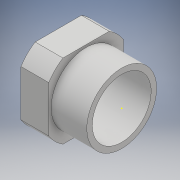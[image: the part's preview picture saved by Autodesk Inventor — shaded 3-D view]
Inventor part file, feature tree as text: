
AUTODESK INVENTOR PART (.ipt)
format: ipt  version: 2018 (Build 220112000, 112)  size: 135,680 bytes
history: native  units: mm
features: sketch x8, extrude x5
ambient origin geometry x8: Origin, YZ Plane, XZ Plane, XY Plane, X Axis, Y Axis, Z Axis, Center Point
bodies: Solid1 (feature_tree)
feature tree (13):
  extrude  "Extrusion1"  Depth=20.4mm
  extrude  "Extrusion2"  Depth=7.6mm
  extrude  "Extrusion3"  Depth=7.6mm
  extrude  "Extrusion4"  Depth=9.75mm
  sketch  "Sketch5"  dims[d11=12.75mm d12=0.0mm d13=6.35mm]
  sketch  "Sketch6"  dims[d14=12.75mm d15=0.0mm]
  extrude  "Extrusion5"  Depth=12.75mm
  sketch  "Sketch8"
  sketch  "Sketch1"  dims[d0=20.4mm d1=20.4mm]
  sketch  "Sketch2"  dims[d2=7.6mm d3=0.0mm d4=24.0mm]
  sketch  "Sketch3"  dims[d5=7.6mm d6=0.0mm d7=19.1mm]
  sketch  "Sketch4"  dims[d8=9.75mm d9=0.0mm d10=16.1mm]
  sketch  "Sketch7"
